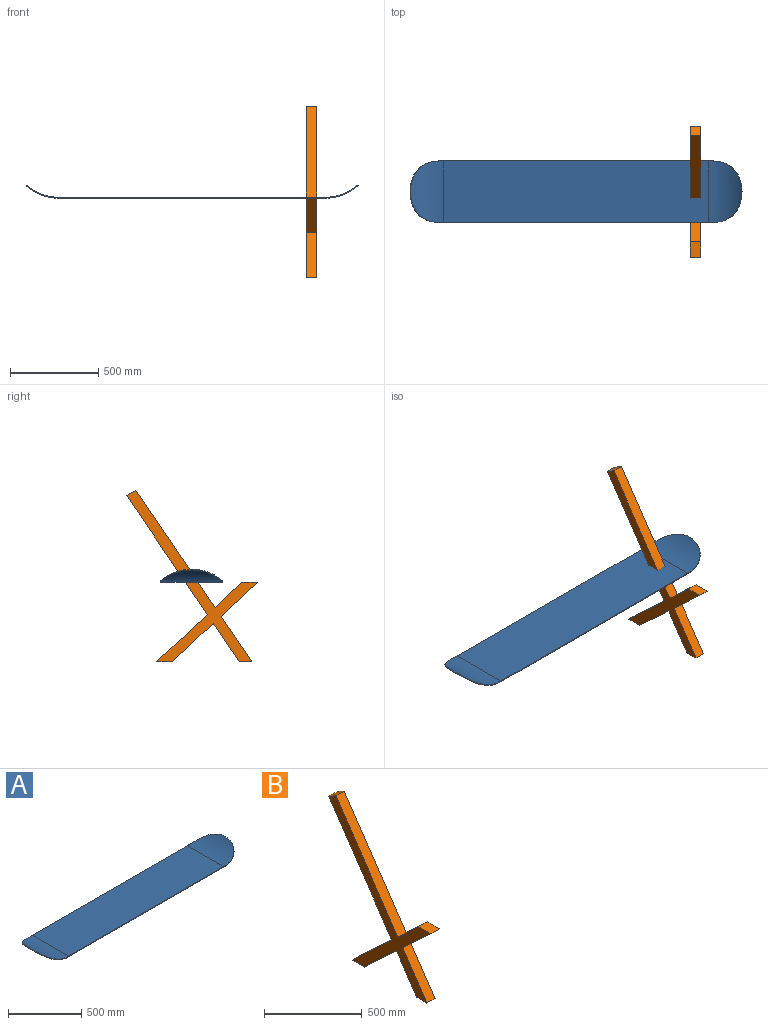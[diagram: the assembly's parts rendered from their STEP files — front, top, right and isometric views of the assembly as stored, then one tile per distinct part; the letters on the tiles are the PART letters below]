
ASSEMBLY  parts=2 mates=1
PART A: 14 faces, bbox 1885.7x350x159.2 mm
  f0: plane 1500x350mm, normal (0,0,1), area 525000mm2, adj f1,f5,f6,f9
  f1: cylinder r=295mm len=350mm, axis (0,1,0), area 58878.8mm2, adj f0,f2,f5,f6,f7,f8
  f2: plane 3.83x3.21mm, normal (-0.77,0,0.64), area 10mm2, adj f1,f3,f7,f8
  f3: cylinder r=300mm len=350mm, axis (0,1,0), area 60107.9mm2, adj f2,f4,f5,f6,f7,f8
  f4: plane 1500x350mm, normal (0,0,-1), area 525000mm2, adj f3,f5,f6,f11
  f5: plane 1547.59x5.67mm, normal (0,-1,0), area 7718.4mm2, adj f0,f1,f3,f4,f8,f9,f11,f13
  f6: plane 1547.59x5.67mm, normal (0,1,0), area 7718.4mm2, adj f0,f1,f3,f4,f7,f9,f11,f12
  f7: cylinder r=174mm len=174mm, axis (-0.64,0,-0.77), area 1430mm2, adj f1,f2,f3,f6
  f8: cylinder r=174mm len=174mm, axis (0.64,0,0.77), area 1429.2mm2, adj f1,f2,f3,f5
  f9: cylinder r=295mm len=350mm, axis (0,1,0), area 58880.1mm2, adj f0,f5,f6,f10,f12,f13
  f10: plane 3.83x3.21mm, normal (0.77,0,0.64), area 10mm2, adj f9,f11,f12,f13
  f11: cylinder r=300mm len=350mm, axis (0,1,0), area 60109.3mm2, adj f4,f5,f6,f10,f12,f13
  f12: cylinder r=174mm len=174mm, axis (0.64,0,-0.77), area 1429.5mm2, adj f6,f9,f10,f11
  f13: cylinder r=174mm len=174mm, axis (-0.64,0,0.77), area 1429.5mm2, adj f5,f9,f10,f11
PART B: 14 faces, bbox 60x740.8x971.9 mm
  f0: plane 286.35x267.3mm, normal (0,0.68,0.73), area 23503.1mm2, adj f1,f11,f12,f13
  f1: plane 674.54x457.19mm, normal (0,0.83,-0.56), area 48892.6mm2, adj f0,f2,f12,f13
  f2: plane 60x52.09mm, normal (0,0.5,0.87), area 3609.3mm2, adj f1,f3,f12,f13
  f3: plane 663.19x449.49mm, normal (0,-0.83,0.56), area 48069.8mm2, adj f2,f4,f12,f13
  f4: plane 151.33x141.26mm, normal (0,0.68,0.73), area 12420.8mm2, adj f3,f5,f12,f13
  f5: plane 87.93x60mm, normal (0,0,1), area 5275.7mm2, adj f4,f6,f12,f13
  f6: plane 205.18x191.53mm, normal (0,-0.68,-0.73), area 16841.2mm2, adj f5,f7,f12,f13
  f7: plane 258.47x175.18mm, normal (0,-0.83,0.56), area 18734.5mm2, adj f6,f8,f12,f13
  f8: plane 72.48x60mm, normal (0,0,-1), area 4349mm2, adj f7,f9,f12,f13
  f9: plane 217.03x147.1mm, normal (0,0.83,-0.56), area 15730.7mm2, adj f8,f10,f12,f13
  f10: plane 232.49x217.03mm, normal (0,-0.68,-0.73), area 19082.8mm2, adj f9,f11,f12,f13
  f11: plane 87.93x60mm, normal (0,0,-1), area 5275.7mm2, adj f0,f10,f12,f13
  f12: plane 971.93x740.84mm, normal (1,0,0), area 105281.6mm2, adj f0,f1,f2,f3,f4,f5,f6,f7
  f13: plane 971.93x740.84mm, normal (-1,0,0), area 105281.6mm2, adj f0,f1,f2,f3,f4,f5,f6,f7
PLACE A t=(0,0,-5)mm
PLACE B t=(678.93,-202.35,-5)mm
MATE planar B.f5 <-> A.f4  axis (0,0,1) through (678.93,-328.39,-5)mm
